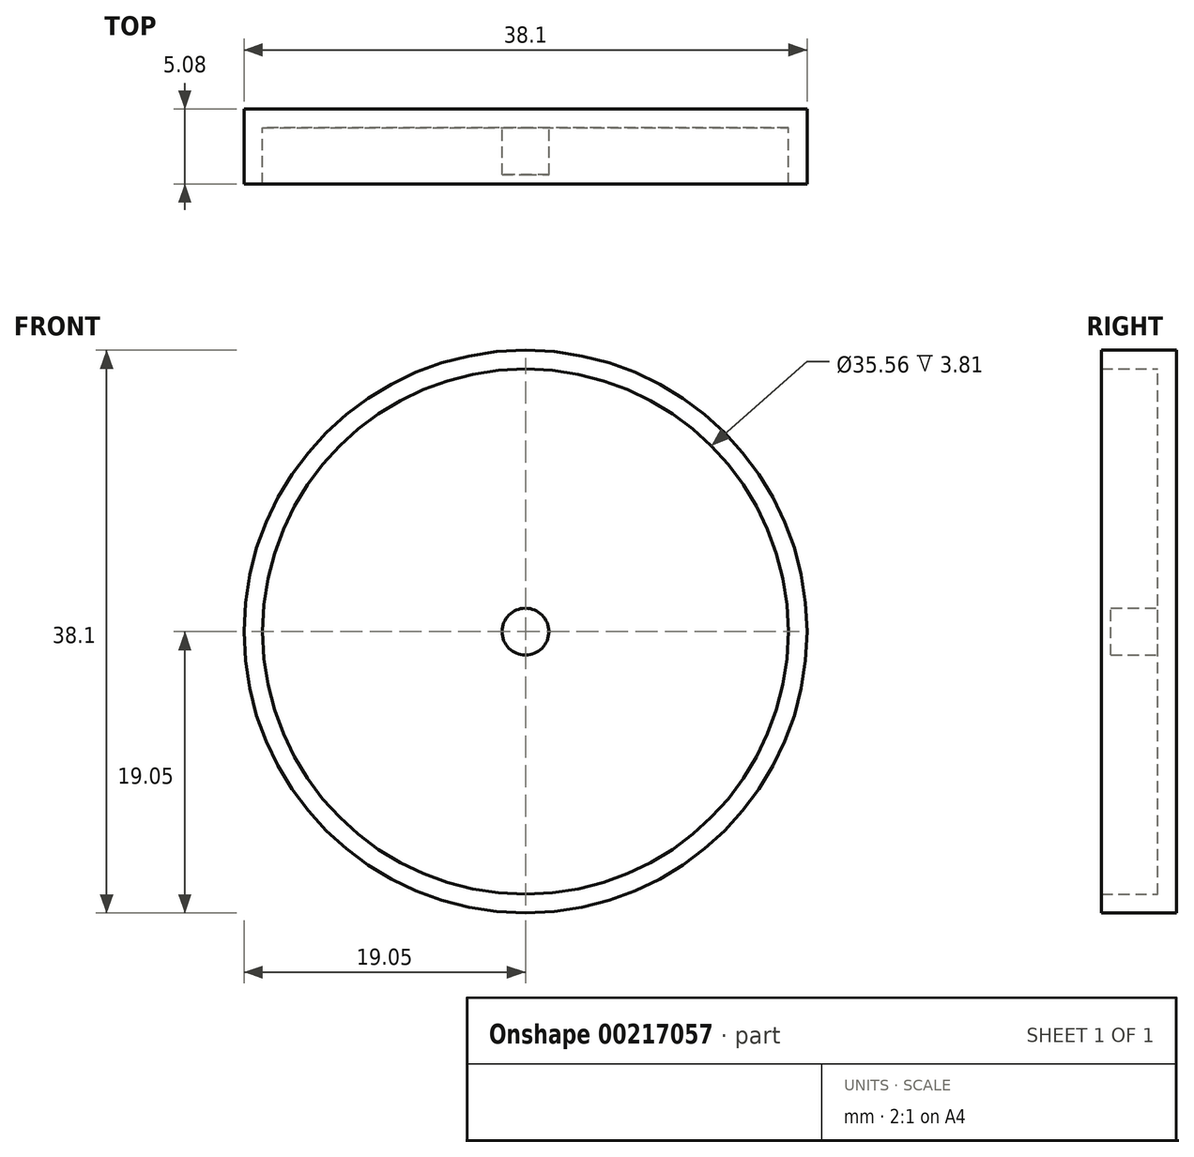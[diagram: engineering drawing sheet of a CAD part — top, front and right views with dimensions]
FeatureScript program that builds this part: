
annotation { "Feature Type Name" : "Feature", "Feature Type Description" : "" }
export const myFeature = defineFeature(function(context is Context, id is Id, definition is map)
    precondition{}
    {
        {
            var Q0;
            Q0=qCreatedBy(makeId("Front.planeOp"),FACE);
            var sketch = newSketch(context, id + "F0", { "sketchPlane" : qUnion([Q0])});
            skCircle(sketch, "E0", {"center": v(0, 0) * mm, "radius": 19.05 * mm});
            skSolve(sketch);
        }
        {
            var Q0;
            Q0 = qSketchRegion(id + "F0", true);
            extrude(context, id + "F1", {"entities" : qUnion([Q0]), "depth" : 5.08 * mm});
        }
        {
            var Q0;
            Q0=makeQuery(id+"F1.opExtrude","CAP_FACE",FACE,{"disambiguationData":[OSD([sQuery(id+"F0.wireOp",EDGE,"E0")])],"isStart":false});
            shell(context, id + "F2", {"entities" : qUnion([Q0]), "thickness" : 1.27 * mm});
        }
        {
            var Q0;
            {var subQ0=sQuery(id+"F0.wireOp",EDGE,"E0");Q0=makeQuery(id+"F2.opShell","OFFSET_FACE",FACE,{"disambiguationData":[OSD([subQ0]),TDD([makeQuery(id+"F1.opExtrude","CAP_FACE",FACE,{"disambiguationData":[OSD([subQ0])],"isStart":true})])]});}
            var sketch = newSketch(context, id + "F3", { "sketchPlane" : qUnion([Q0])});
            skCircle(sketch, "E1", {"center": v(0, 0) * mm, "radius": 1.59 * mm});
            skSolve(sketch);
        }
        {
            var Q0;
            Q0=makeQuery(id+"F3.imprint","IMPRINT",FACE,{"disambiguationData":[TD([[makeQuery(id+"F3.imprint","IMPRINT",EDGE,{"derivedFrom":sQuery(id+"F3.wireOp",EDGE,"E1")}),1.0]])]});
            extrude(context, id + "F4", {"entities" : qUnion([Q0]), "operationType" : NewBodyOperationType.ADD, "depth" : 3.17 * mm});
        }
    });
